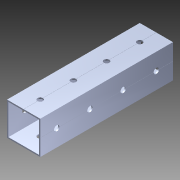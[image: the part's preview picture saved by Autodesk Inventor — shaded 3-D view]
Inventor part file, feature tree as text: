
AUTODESK INVENTOR PART (.ipt)
format: ipt  version: 2014 SP1 (Build 180222100, 222)  size: 1,225,728 bytes
history: native  units: in
note: dims shown in document units (in); Inventor stores cm internally (conversion verified against a paired STEP export)
features: extrude x3, sketch x3, pattern_circular x1, other x1, imported_body x1
ambient origin geometry x8: Origin, YZ Plane, XZ Plane, XY Plane, X Axis, Y Axis, Z Axis, Center Point
bodies: Body1 (feature_tree)
feature tree (9):
  pattern_circular  "CirPattern2"
  other  "1x1 tube1"
  extrude  "Extrusion1"  Depth=4.0in TaperAngle=0.0deg
  extrude  "Extrusion2"  [1 undecoded]
  extrude  "Extrusion3"  [1 undecoded]
  imported_body  "Base1"
  sketch  "Sketch1"  dims[d0=50.0in d1=0.0in d2=4.0in d3=0.0in]
  sketch  "Sketch3"  dims[d4=1.0in d5=0.0in]
  sketch  "Sketch4"
note: 2 required parameter values undecoded (feature->parameter linkage not recoverable at this tier; creation-order binding heuristic only, values carry confidence <= 0.55)
